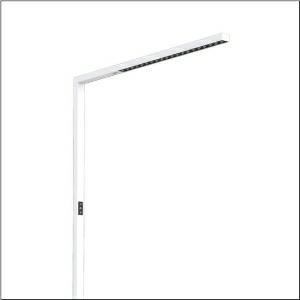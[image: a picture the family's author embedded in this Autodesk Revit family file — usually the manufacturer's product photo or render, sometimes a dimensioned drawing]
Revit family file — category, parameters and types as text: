
# Revit family: silica_31_floor_51my52fatcw
name_source: partatom
category: Lighting Fixtures
units: mm (PartAtom-declared; Revit-internal decimal feet)

## family parameters
Cut with Voids When Loaded = No
Host = Face
Light Source = No
Part Type = Normal
Room Calculation Point = No
Round Connector Dimension = Use Diameter
Shared = No

## types (1)
- --- (1 x LED, 8520 lm, 71 W, 4000K)
    Apparent Load = 71 VA
    CIE Flux Codes = 86 100 100 24 100
    Color Rendering = 80
    Color Temperature = 4000K
    Default Elevation = 1800 mm
    Description = Silica® 31 Floor, floorstanding luminaire, secondary optical cover: cover panel, of PMMA, light emission: direct/indirect distribution, primary light characteristic: symmetric, installation type: not mounted, LED, rated luminous flux: 8.520lm, luminous efficacy: 120lm/W, light colour: 8tw, colour temperature: 2700..6500K, control gear: Touchdim, daylight-dependent control, with cable with plug, mains connection: 230V, AC, 50Hz, connection cable included, cable length: 2,5m, rated input power: 71W, luminaire head, of aluminium, traffic white (RAL 9016), length: 1.203mm, width: 52mm, supporting column, angular, of aluminium, traffic white (RAL 9016), baseplate, of steel, traffic white (RAL 9016), local control - self-sufficient standalone sensors, direct and indirect component separately switchable, protection rating (complete): IP20, insulation class (complete): insulation class I (protective earthing), certification: CE, ENEC, permissible operating ambient temperature: -20..+40°C, standard: EN 50419, packaging unit: 1 piece
    Height = 36 mm
    Lamp = 1 x LED
    Lamp Light Flux = 8520 lm
    Lamp Power = 71 W
    Lamp count = 1
    Length = 1203 mm
    Luminous efficacy = 120 lm/W
    Manufacturer = Siteco
    ModVariant = No
    Model = 51MY52FATCW
    Mounting Place = Floor
    Mounting Type = Freestanding
    Number of Poles = 1
    OnlyDefault = Yes
    Power Factor = 1
    Product Name = Silica 31 Floor
    Product group = floorstanding luminaire
    ProductGroupID = 1302
    Protection Class = Protection class I
    Protection Degree = IP 20
    RLX_Detail_Level = 1
    RLX_Emergency_Light_Flux = 0 lm
    RLX_Emergency_Type = 0
    RLX_Emergency_Type_DB = No
    RlxData = <blob elided: 17269 chars, md5=41a99a68>
    Socket = socket
    Standby Power = 0 W
    System Light Flux = 8520 lm
    System Power = 71 W
    Type Comments = factory setting
    Type Image = l_1275309.jpg
    URL = http://relux.com
    VarID = @adj_087091
    Voltage = 0 V
    Weight = 0.00 kg
    Width = 52 mm  [stored 0.170604 ft]

note: [stored X ft] marks values corroborated as IEEE doubles in the binary element streams (Revit-internal decimal feet)

## geometry (parser evidence)
native form markers: Blend x4, Sweep x16
no freeform markers — native parametric forms only
